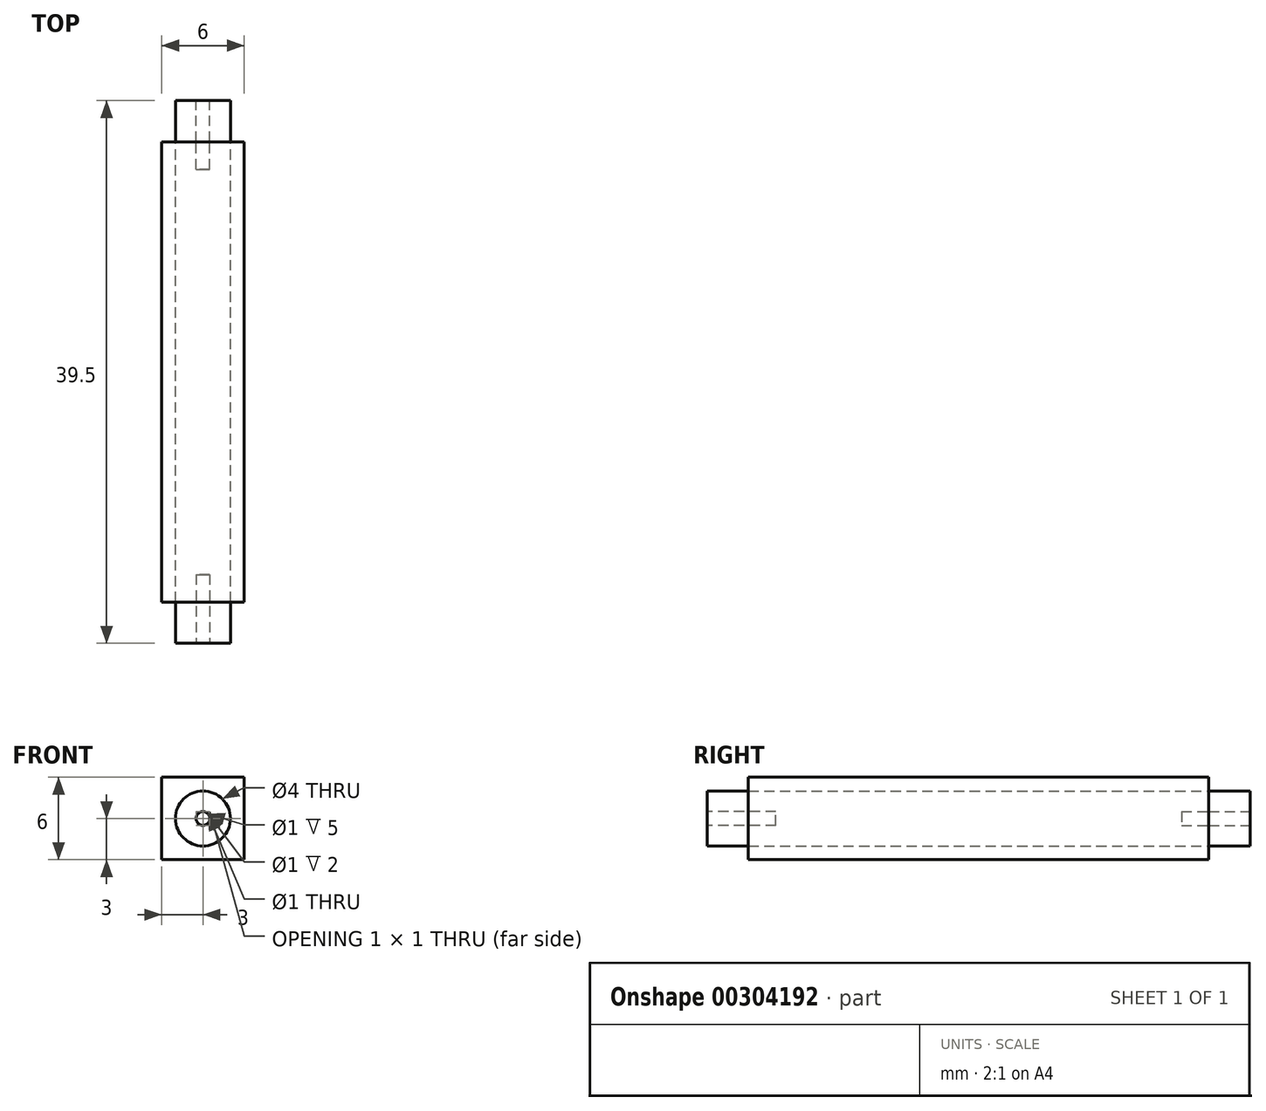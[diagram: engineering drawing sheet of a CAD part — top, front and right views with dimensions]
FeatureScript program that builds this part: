
annotation { "Feature Type Name" : "Feature", "Feature Type Description" : "" }
export const myFeature = defineFeature(function(context is Context, id is Id, definition is map)
    precondition{}
    {
        {
            var Q0;
            Q0=qCreatedBy(makeId("Front.planeOp"),FACE);
            var sketch = newSketch(context, id + "F0", { "sketchPlane" : qUnion([Q0])});
            skCircle(sketch, "E0", {"center": v(0, 0) * mm, "radius": 2 * mm});
            skSolve(sketch);
        }
        {
            var Q0;
            Q0=makeQuery(id+"F0.imprint","IMPRINT",FACE,{"disambiguationData":[TD([[makeQuery(id+"F0.imprint","IMPRINT",EDGE,{"derivedFrom":sQuery(id+"F0.wireOp",EDGE,"E0")}),1.0]])]});
            extrude(context, id + "F1", {"entities" : qUnion([Q0]), "depth" : 3 * mm});
        }
        {
            var Q0;
            Q0=makeQuery(id+"F1.opExtrude","CAP_FACE",FACE,{"disambiguationData":[OSD([sQuery(id+"F0.wireOp",EDGE,"E0")])],"isStart":false});
            var sketch = newSketch(context, id + "F2", { "sketchPlane" : qUnion([Q0])});
            skLineSegment(sketch, "E1.bottom", {"start": v(-3, 3) * mm, "end": v(3, 3) * mm});
            skLineSegment(sketch, "E1.top", {"start": v(-3, -3) * mm, "end": v(3, -3) * mm});
            skLineSegment(sketch, "E1.left", {"start": v(-3, 3) * mm, "end": v(-3, -3) * mm});
            skLineSegment(sketch, "E1.right", {"start": v(3, 3) * mm, "end": v(3, -3) * mm});
            skPoint(sketch, "E1.middle", {"position": v(0, 0) * mm});
            skSolve(sketch);
        }
        {
            var Q0;
            Q0=makeQuery(id+"F2.imprint","IMPRINT",FACE,{"disambiguationData":[TD([[makeQuery(id+"F2.imprint","IMPRINT",EDGE,{"derivedFrom":sQuery(id+"F2.wireOp",EDGE,"E1.bottom")}),-1.0]])]});
            extrude(context, id + "F3", {"entities" : qUnion([Q0]), "depth" : 33.5 * mm});
        }
        {
            var Q0;
            Q0=makeQuery(id+"F1.opExtrude","CAP_FACE",FACE,{"disambiguationData":[OSD([sQuery(id+"F0.wireOp",EDGE,"E0")])],"isStart":false});
            extrude(context, id + "F4", {"entities" : qUnion([Q0]), "depth" : 36.5 * mm});
        }
        {
            var Q0;
            Q0=makeQuery(id+"F4.opExtrude","CAP_FACE",FACE,{"disambiguationData":[OSD([sQuery(id+"F0.wireOp",EDGE,"E0")])],"isStart":false});
            var sketch = newSketch(context, id + "F5", { "sketchPlane" : qUnion([Q0])});
            skCircle(sketch, "E2", {"center": v(0, 0) * mm, "radius": 0.5 * mm});
            skSolve(sketch);
        }
        {
            var Q0;
            Q0=makeQuery(id+"F5.imprint","IMPRINT",FACE,{"disambiguationData":[TD([[makeQuery(id+"F5.imprint","IMPRINT",EDGE,{"derivedFrom":sQuery(id+"F5.wireOp",EDGE,"E2")}),1.0]])]});
            extrude(context, id + "F6", {"entities" : qUnion([Q0]), "operationType" : NewBodyOperationType.REMOVE, "oppositeDirection" : true, "depth" : 5 * mm});
        }
        {
            var Q0;
            Q0=makeQuery(id+"F1.opExtrude","CAP_FACE",FACE,{"disambiguationData":[OSD([sQuery(id+"F0.wireOp",EDGE,"E0")])],"isStart":true});
            var sketch = newSketch(context, id + "F7", { "sketchPlane" : qUnion([Q0])});
            skCircle(sketch, "E3", {"center": v(0, 0) * mm, "radius": 0.5 * mm});
            skSolve(sketch);
        }
        {
            var Q0;
            Q0=makeQuery(id+"F7.imprint","IMPRINT",FACE,{"disambiguationData":[TD([[makeQuery(id+"F7.imprint","IMPRINT",EDGE,{"derivedFrom":sQuery(id+"F7.wireOp",EDGE,"E3")}),1.0]])]});
            extrude(context, id + "F8", {"entities" : qUnion([Q0]), "operationType" : NewBodyOperationType.REMOVE, "oppositeDirection" : true, "depth" : 5 * mm});
        }
    });
